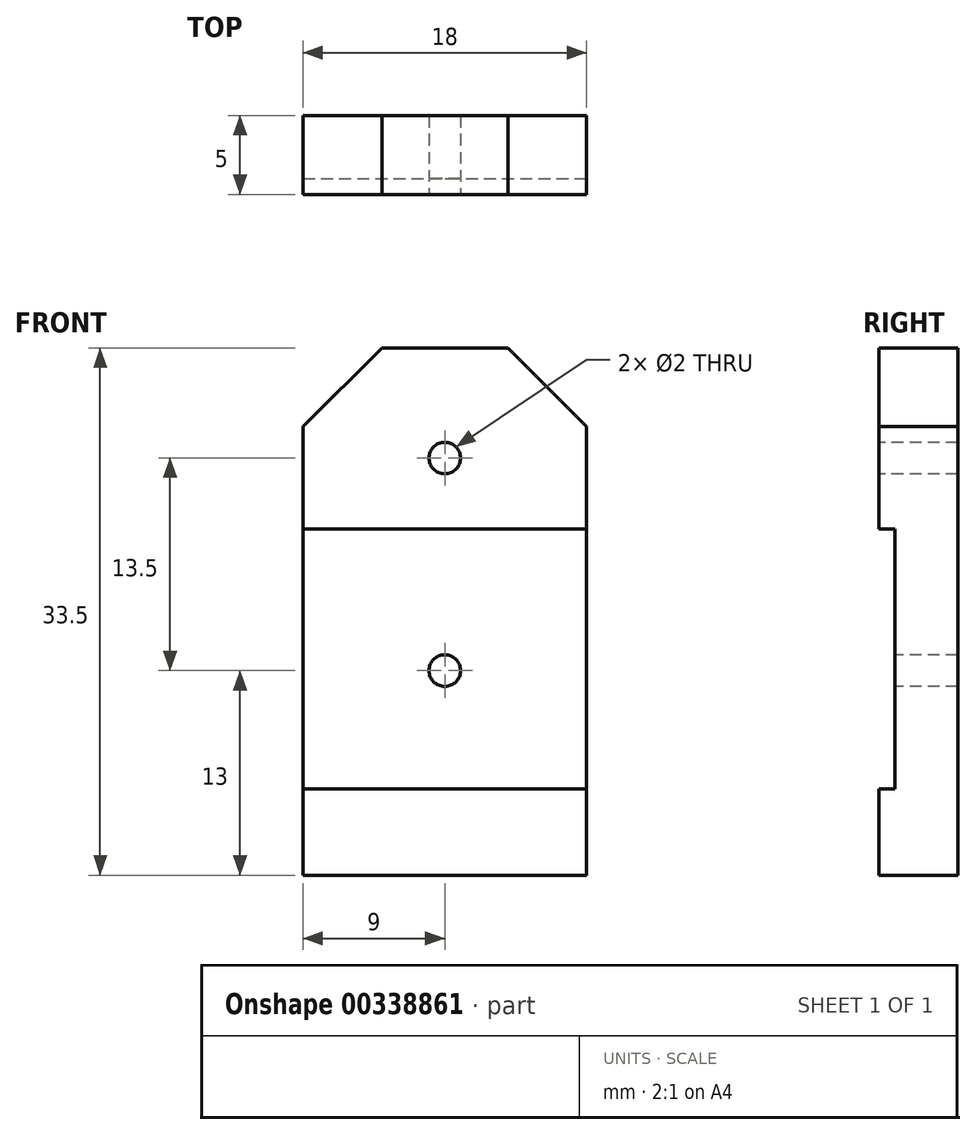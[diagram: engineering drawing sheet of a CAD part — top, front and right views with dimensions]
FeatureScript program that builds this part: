
annotation { "Feature Type Name" : "Feature", "Feature Type Description" : "" }
export const myFeature = defineFeature(function(context is Context, id is Id, definition is map)
    precondition{}
    {
        {
            var Q0;
            Q0=qCreatedBy(makeId("Front.planeOp"),FACE);
            var sketch = newSketch(context, id + "F0", { "sketchPlane" : qUnion([Q0])});
            skLineSegment(sketch, "E0", {"start": v(0, 0) * mm, "end": v(18, 0) * mm});
            skLineSegment(sketch, "E1", {"start": v(18, 0) * mm, "end": v(18, 28.5) * mm});
            skLineSegment(sketch, "E2", {"start": v(18, 28.5) * mm, "end": v(13, 33.5) * mm});
            skLineSegment(sketch, "E3", {"start": v(13, 33.5) * mm, "end": v(5, 33.5) * mm});
            skLineSegment(sketch, "E4", {"start": v(5, 33.5) * mm, "end": v(0, 28.5) * mm});
            skLineSegment(sketch, "E5", {"start": v(0, 28.5) * mm, "end": v(0, 0) * mm});
            skSolve(sketch);
        }
        {
            var Q0;
            Q0 = qSketchRegion(id + "F0", true);
            extrude(context, id + "F1", {"entities" : qUnion([Q0]), "depth" : 5 * mm});
        }
        {
            var Q0;
            Q0=makeQuery(id+"F1.opExtrude","CAP_FACE",FACE,{"disambiguationData":[OSD([sQuery(id+"F0.wireOp",EDGE,"E0"),sQuery(id+"F0.wireOp",EDGE,"E1"),sQuery(id+"F0.wireOp",EDGE,"E2"),sQuery(id+"F0.wireOp",EDGE,"E3"),sQuery(id+"F0.wireOp",EDGE,"E4"),sQuery(id+"F0.wireOp",EDGE,"E5")])],"isStart":false});
            var sketch = newSketch(context, id + "F2", { "sketchPlane" : qUnion([Q0])});
            skLineSegment(sketch, "E6.bottom", {"start": v(0, 5.5) * mm, "end": v(18, 5.5) * mm});
            skLineSegment(sketch, "E6.top", {"start": v(0, 22) * mm, "end": v(18, 22) * mm});
            skLineSegment(sketch, "E6.left", {"start": v(0, 5.5) * mm, "end": v(0, 22) * mm});
            skLineSegment(sketch, "E6.right", {"start": v(18, 5.5) * mm, "end": v(18, 22) * mm});
            skSolve(sketch);
        }
        {
            var Q0;
            Q0 = qSketchRegion(id + "F2", true);
            extrude(context, id + "F3", {"entities" : qUnion([Q0]), "operationType" : NewBodyOperationType.REMOVE, "oppositeDirection" : true, "depth" : 1 * mm});
        }
        {
            var Q0;
            {var subQ0=sQuery(id+"F0.wireOp",EDGE,"E4");var subQ1=sQuery(id+"F0.wireOp",EDGE,"E3");var subQ2=sQuery(id+"F0.wireOp",EDGE,"E2");var subQ3=sQuery(id+"F0.wireOp",EDGE,"E1");var subQ4=sQuery(id+"F0.wireOp",EDGE,"E5");Q0=makeQuery(id+"F3.boolean.opBoolean","SPLIT",FACE,{"disambiguationData":[TD([makeQuery(id+"F1.opExtrude","SWEPT_FACE",FACE,{"disambiguationData":[OSD([subQ2])]})])],"derivedFrom":makeQuery(id+"F1.opExtrude","CAP_FACE",FACE,{"disambiguationData":[OSD([sQuery(id+"F0.wireOp",EDGE,"E0"),subQ3,subQ2,subQ1,subQ0,subQ4])],"isStart":false})});}
            var sketch = newSketch(context, id + "F4", { "sketchPlane" : qUnion([Q0])});
            skCircle(sketch, "E7", {"center": v(9, 26.5) * mm, "radius": 1 * mm});
            skSolve(sketch);
        }
        {
            var Q0;
            Q0 = qSketchRegion(id + "F4", true);
            extrude(context, id + "F5", {"entities" : qUnion([Q0]), "operationType" : NewBodyOperationType.REMOVE, "endBound" : BoundingType.THROUGH_ALL, "oppositeDirection" : true, "depth" : 25 * mm});
        }
        {
            var Q0;
            Q0=makeQuery(id+"F3.boolean.opBoolean","COPY",FACE,{"derivedFrom":makeQuery(id+"F3.opExtrude","CAP_FACE",FACE,{"disambiguationData":[OSD([sQuery(id+"F2.wireOp",EDGE,"E6.bottom"),sQuery(id+"F2.wireOp",EDGE,"E6.top"),sQuery(id+"F2.wireOp",EDGE,"E6.left"),sQuery(id+"F2.wireOp",EDGE,"E6.right")])],"isStart":false})});
            var sketch = newSketch(context, id + "F6", { "sketchPlane" : qUnion([Q0])});
            skCircle(sketch, "E8", {"center": v(9, 13) * mm, "radius": 1 * mm});
            skSolve(sketch);
        }
        {
            var Q0;
            Q0 = qSketchRegion(id + "F6", true);
            extrude(context, id + "F7", {"entities" : qUnion([Q0]), "operationType" : NewBodyOperationType.REMOVE, "endBound" : BoundingType.THROUGH_ALL, "oppositeDirection" : true, "depth" : 25 * mm});
        }
    });
